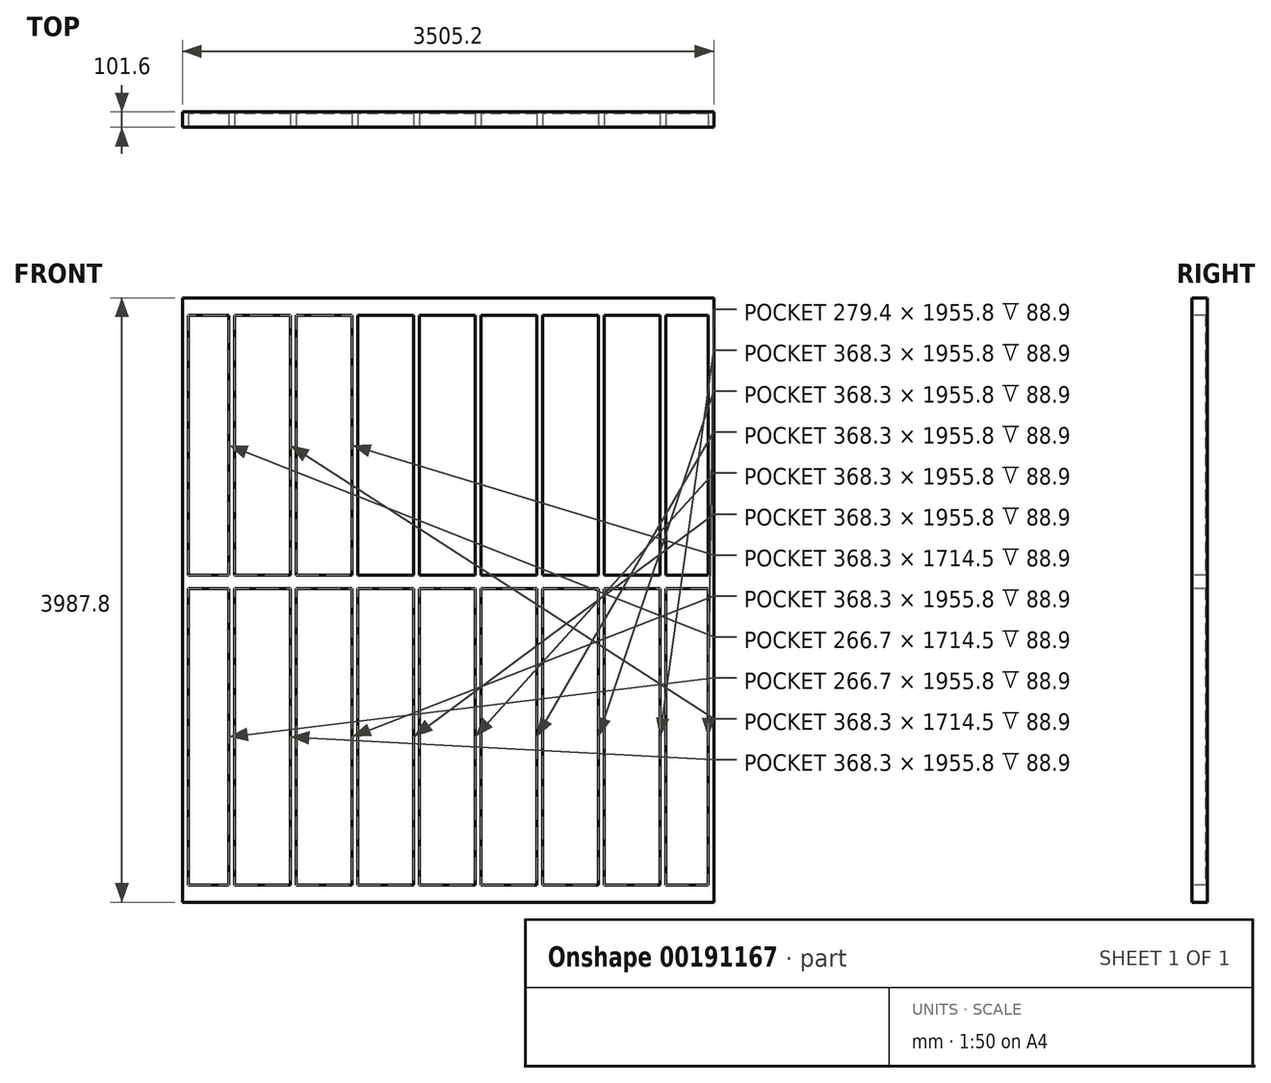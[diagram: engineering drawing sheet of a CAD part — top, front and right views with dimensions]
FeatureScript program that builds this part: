
annotation { "Feature Type Name" : "Feature", "Feature Type Description" : "" }
export const myFeature = defineFeature(function(context is Context, id is Id, definition is map)
    precondition{}
    {
        {
            var Q0;
            Q0=qCreatedBy(makeId("Top.planeOp"),FACE);
            var sketch = newSketch(context, id + "F0", { "sketchPlane" : qUnion([Q0])});
            skLineSegment(sketch, "E0.bottom", {"start": v(1752.6, -44.45) * mm, "end": v(-1752.6, -44.45) * mm});
            skLineSegment(sketch, "E0.top", {"start": v(1752.6, 44.45) * mm, "end": v(-1752.6, 44.45) * mm});
            skLineSegment(sketch, "E0.left", {"start": v(1752.6, -44.45) * mm, "end": v(1752.6, 44.45) * mm});
            skLineSegment(sketch, "E0.right", {"start": v(-1752.6, -44.45) * mm, "end": v(-1752.6, 44.45) * mm});
            skPoint(sketch, "E0.middle", {"position": v(0, 0) * mm});
            skSolve(sketch);
        }
        {
            var Q0;
            Q0 = qSketchRegion(id + "F0", true);
            extrude(context, id + "F1", {"entities" : qUnion([Q0]), "depth" : 38.1 * mm});
        }
        {
            var Q0;
            Q0=makeQuery(id+"F1.opExtrude","CAP_FACE",FACE,{"disambiguationData":[OSD([sQuery(id+"F0.wireOp",EDGE,"E0.bottom"),sQuery(id+"F0.wireOp",EDGE,"E0.top"),sQuery(id+"F0.wireOp",EDGE,"E0.left"),sQuery(id+"F0.wireOp",EDGE,"E0.right")])],"isStart":false});
            var sketch = newSketch(context, id + "F2", { "sketchPlane" : qUnion([Q0])});
            skLineSegment(sketch, "E1.bottom", {"start": v(1752.6, 44.45) * mm, "end": v(1714.5, 44.45) * mm});
            skLineSegment(sketch, "E1.top", {"start": v(1752.6, -44.45) * mm, "end": v(1714.5, -44.45) * mm});
            skLineSegment(sketch, "E1.left", {"start": v(1752.6, 44.45) * mm, "end": v(1752.6, -44.45) * mm});
            skLineSegment(sketch, "E1.right", {"start": v(1714.5, 44.45) * mm, "end": v(1714.5, -44.45) * mm});
            skLineSegment(sketch, "E2.bottom", {"start": v(1435.1, 44.45) * mm, "end": v(1397, 44.45) * mm});
            skLineSegment(sketch, "E2.top", {"start": v(1435.1, -44.45) * mm, "end": v(1397, -44.45) * mm});
            skLineSegment(sketch, "E2.left", {"start": v(1435.1, 44.45) * mm, "end": v(1435.1, -44.45) * mm});
            skLineSegment(sketch, "E2.right", {"start": v(1397, 44.45) * mm, "end": v(1397, -44.45) * mm});
            skLineSegment(sketch, "E3.bottom", {"start": v(1028.7, 44.45) * mm, "end": v(990.6, 44.45) * mm});
            skLineSegment(sketch, "E3.top", {"start": v(1028.7, -44.45) * mm, "end": v(990.6, -44.45) * mm});
            skLineSegment(sketch, "E3.left", {"start": v(1028.7, 44.45) * mm, "end": v(1028.7, -44.45) * mm});
            skLineSegment(sketch, "E3.right", {"start": v(990.6, 44.45) * mm, "end": v(990.6, -44.45) * mm});
            skLineSegment(sketch, "E4.bottom", {"start": v(622.3, 44.45) * mm, "end": v(584.2, 44.45) * mm});
            skLineSegment(sketch, "E4.top", {"start": v(622.3, -44.45) * mm, "end": v(584.2, -44.45) * mm});
            skLineSegment(sketch, "E4.left", {"start": v(622.3, 44.45) * mm, "end": v(622.3, -44.45) * mm});
            skLineSegment(sketch, "E4.right", {"start": v(584.2, 44.45) * mm, "end": v(584.2, -44.45) * mm});
            skLineSegment(sketch, "E5.bottom", {"start": v(215.9, 44.45) * mm, "end": v(177.8, 44.45) * mm});
            skLineSegment(sketch, "E5.top", {"start": v(215.9, -44.45) * mm, "end": v(177.8, -44.45) * mm});
            skLineSegment(sketch, "E5.left", {"start": v(215.9, 44.45) * mm, "end": v(215.9, -44.45) * mm});
            skLineSegment(sketch, "E5.right", {"start": v(177.8, 44.45) * mm, "end": v(177.8, -44.45) * mm});
            skLineSegment(sketch, "E6.bottom", {"start": v(-190.5, 44.45) * mm, "end": v(-228.6, 44.45) * mm});
            skLineSegment(sketch, "E6.top", {"start": v(-190.5, -44.45) * mm, "end": v(-228.6, -44.45) * mm});
            skLineSegment(sketch, "E6.left", {"start": v(-190.5, 44.45) * mm, "end": v(-190.5, -44.45) * mm});
            skLineSegment(sketch, "E6.right", {"start": v(-228.6, 44.45) * mm, "end": v(-228.6, -44.45) * mm});
            skLineSegment(sketch, "E7.bottom", {"start": v(-596.9, 44.45) * mm, "end": v(-635, 44.45) * mm});
            skLineSegment(sketch, "E7.top", {"start": v(-596.9, -44.45) * mm, "end": v(-635, -44.45) * mm});
            skLineSegment(sketch, "E7.left", {"start": v(-596.9, 44.45) * mm, "end": v(-596.9, -44.45) * mm});
            skLineSegment(sketch, "E7.right", {"start": v(-635, 44.45) * mm, "end": v(-635, -44.45) * mm});
            skLineSegment(sketch, "E8.bottom", {"start": v(-1003.3, 44.45) * mm, "end": v(-1041.4, 44.45) * mm});
            skLineSegment(sketch, "E8.top", {"start": v(-1003.3, -44.45) * mm, "end": v(-1041.4, -44.45) * mm});
            skLineSegment(sketch, "E8.left", {"start": v(-1003.3, 44.45) * mm, "end": v(-1003.3, -44.45) * mm});
            skLineSegment(sketch, "E8.right", {"start": v(-1041.4, 44.45) * mm, "end": v(-1041.4, -44.45) * mm});
            skLineSegment(sketch, "E9.bottom", {"start": v(-1752.6, 44.45) * mm, "end": v(-1714.5, 44.45) * mm});
            skLineSegment(sketch, "E9.top", {"start": v(-1752.6, -44.45) * mm, "end": v(-1714.5, -44.45) * mm});
            skLineSegment(sketch, "E9.left", {"start": v(-1752.6, 44.45) * mm, "end": v(-1752.6, -44.45) * mm});
            skLineSegment(sketch, "E9.right", {"start": v(-1714.5, 44.45) * mm, "end": v(-1714.5, -44.45) * mm});
            skLineSegment(sketch, "E10.bottom", {"start": v(-1447.8, 44.45) * mm, "end": v(-1409.7, 44.45) * mm});
            skLineSegment(sketch, "E10.top", {"start": v(-1447.8, -44.45) * mm, "end": v(-1409.7, -44.45) * mm});
            skLineSegment(sketch, "E10.left", {"start": v(-1447.8, 44.45) * mm, "end": v(-1447.8, -44.45) * mm});
            skLineSegment(sketch, "E10.right", {"start": v(-1409.7, 44.45) * mm, "end": v(-1409.7, -44.45) * mm});
            skSolve(sketch);
        }
        {
            var Q0;
            Q0 = qSketchRegion(id + "F2", true);
            extrude(context, id + "F3", {"entities" : qUnion([Q0]), "operationType" : NewBodyOperationType.ADD, "depth" : 3759.2 * mm});
        }
        {
            var Q0;
            Q0=makeQuery(id+"F1.opExtrude","CAP_FACE",FACE,{"disambiguationData":[OSD([sQuery(id+"F0.wireOp",EDGE,"E0.bottom"),sQuery(id+"F0.wireOp",EDGE,"E0.top"),sQuery(id+"F0.wireOp",EDGE,"E0.left"),sQuery(id+"F0.wireOp",EDGE,"E0.right")])],"isStart":true});
            var sketch = newSketch(context, id + "F4", { "sketchPlane" : qUnion([Q0])});
            skLineSegment(sketch, "E11.bottom", {"start": v(1752.6, -44.45) * mm, "end": v(-1752.6, -44.45) * mm});
            skLineSegment(sketch, "E11.top", {"start": v(1752.6, 44.45) * mm, "end": v(-1752.6, 44.45) * mm});
            skLineSegment(sketch, "E11.left", {"start": v(1752.6, -44.45) * mm, "end": v(1752.6, 44.45) * mm});
            skLineSegment(sketch, "E11.right", {"start": v(-1752.6, -44.45) * mm, "end": v(-1752.6, 44.45) * mm});
            skSolve(sketch);
        }
        {
            var Q0;
            Q0 = qSketchRegion(id + "F4", true);
            extrude(context, id + "F5", {"entities" : qUnion([Q0]), "operationType" : NewBodyOperationType.ADD, "depth" : 76.2 * mm});
        }
        {
            var Q0;
            Q0=makeQuery(id+"F5.boolean.opBoolean","MERGE",FACE,{"derivedFrom":[makeQuery(id+"F3.boolean.opBoolean","MERGE",FACE,{"derivedFrom":[makeQuery(id+"F1.opExtrude","SWEPT_FACE",FACE,{"disambiguationData":[OSD([sQuery(id+"F0.wireOp",EDGE,"E0.top")])]}),makeQuery(id+"F3.opExtrude","SWEPT_FACE",FACE,{"disambiguationData":[OSD([sQuery(id+"F2.wireOp",EDGE,"E1.bottom")])]}),makeQuery(id+"F3.opExtrude","SWEPT_FACE",FACE,{"disambiguationData":[OSD([sQuery(id+"F2.wireOp",EDGE,"E2.bottom")])]}),makeQuery(id+"F3.opExtrude","SWEPT_FACE",FACE,{"disambiguationData":[OSD([sQuery(id+"F2.wireOp",EDGE,"E3.bottom")])]}),makeQuery(id+"F3.opExtrude","SWEPT_FACE",FACE,{"disambiguationData":[OSD([sQuery(id+"F2.wireOp",EDGE,"E4.bottom")])]}),makeQuery(id+"F3.opExtrude","SWEPT_FACE",FACE,{"disambiguationData":[OSD([sQuery(id+"F2.wireOp",EDGE,"E5.bottom")])]}),makeQuery(id+"F3.opExtrude","SWEPT_FACE",FACE,{"disambiguationData":[OSD([sQuery(id+"F2.wireOp",EDGE,"E6.bottom")])]}),makeQuery(id+"F3.opExtrude","SWEPT_FACE",FACE,{"disambiguationData":[OSD([sQuery(id+"F2.wireOp",EDGE,"E7.bottom")])]}),makeQuery(id+"F3.opExtrude","SWEPT_FACE",FACE,{"disambiguationData":[OSD([sQuery(id+"F2.wireOp",EDGE,"E8.bottom")])]}),makeQuery(id+"F3.opExtrude","SWEPT_FACE",FACE,{"disambiguationData":[OSD([sQuery(id+"F2.wireOp",EDGE,"E9.bottom")])]}),makeQuery(id+"F3.opExtrude","SWEPT_FACE",FACE,{"disambiguationData":[OSD([sQuery(id+"F2.wireOp",EDGE,"E10.bottom")])]})]}),makeQuery(id+"F5.opExtrude","SWEPT_FACE",FACE,{"disambiguationData":[OSD([sQuery(id+"F4.wireOp",EDGE,"E11.bottom")])]})]});
            var sketch = newSketch(context, id + "F6", { "sketchPlane" : qUnion([Q0])});
            skLineSegment(sketch, "E12.bottom", {"start": v(1752.6, 3797.3) * mm, "end": v(-1752.6, 3797.3) * mm});
            skLineSegment(sketch, "E12.top", {"start": v(1752.6, 3835.4) * mm, "end": v(-1752.6, 3835.4) * mm});
            skLineSegment(sketch, "E12.left", {"start": v(1752.6, 3797.3) * mm, "end": v(1752.6, 3835.4) * mm});
            skLineSegment(sketch, "E12.right", {"start": v(-1752.6, 3797.3) * mm, "end": v(-1752.6, 3835.4) * mm});
            skSolve(sketch);
        }
        {
            var Q0;
            Q0 = qSketchRegion(id + "F6", true);
            extrude(context, id + "F7", {"entities" : qUnion([Q0]), "operationType" : NewBodyOperationType.ADD, "oppositeDirection" : true, "depth" : 88.9 * mm});
        }
        {
            var Q0;
            Q0=makeQuery(id+"F7.opExtrude","SWEPT_FACE",FACE,{"disambiguationData":[OSD([sQuery(id+"F6.wireOp",EDGE,"E12.top")])]});
            var sketch = newSketch(context, id + "F8", { "sketchPlane" : qUnion([Q0])});
            skLineSegment(sketch, "E13.bottom", {"start": v(-1752.6, -44.45) * mm, "end": v(1752.6, -44.45) * mm});
            skLineSegment(sketch, "E13.top", {"start": v(-1752.6, 44.45) * mm, "end": v(1752.6, 44.45) * mm});
            skLineSegment(sketch, "E13.left", {"start": v(-1752.6, -44.45) * mm, "end": v(-1752.6, 44.45) * mm});
            skLineSegment(sketch, "E13.right", {"start": v(1752.6, -44.45) * mm, "end": v(1752.6, 44.45) * mm});
            skSolve(sketch);
        }
        {
            var Q0;
            Q0 = qSketchRegion(id + "F8", true);
            extrude(context, id + "F9", {"entities" : qUnion([Q0]), "operationType" : NewBodyOperationType.ADD, "depth" : 76.2 * mm});
        }
        {
            var Q0;
            Q0=makeQuery(id+"F9.boolean.opBoolean","MERGE",FACE,{"derivedFrom":[makeQuery(id+"F7.boolean.opBoolean","MERGE",FACE,{"derivedFrom":[makeQuery(id+"F5.boolean.opBoolean","MERGE",FACE,{"derivedFrom":[makeQuery(id+"F3.boolean.opBoolean","MERGE",FACE,{"derivedFrom":[makeQuery(id+"F1.opExtrude","SWEPT_FACE",FACE,{"disambiguationData":[OSD([sQuery(id+"F0.wireOp",EDGE,"E0.bottom")])]}),makeQuery(id+"F3.opExtrude","SWEPT_FACE",FACE,{"disambiguationData":[OSD([sQuery(id+"F2.wireOp",EDGE,"E1.top")])]}),makeQuery(id+"F3.opExtrude","SWEPT_FACE",FACE,{"disambiguationData":[OSD([sQuery(id+"F2.wireOp",EDGE,"E2.top")])]}),makeQuery(id+"F3.opExtrude","SWEPT_FACE",FACE,{"disambiguationData":[OSD([sQuery(id+"F2.wireOp",EDGE,"E3.top")])]}),makeQuery(id+"F3.opExtrude","SWEPT_FACE",FACE,{"disambiguationData":[OSD([sQuery(id+"F2.wireOp",EDGE,"E4.top")])]}),makeQuery(id+"F3.opExtrude","SWEPT_FACE",FACE,{"disambiguationData":[OSD([sQuery(id+"F2.wireOp",EDGE,"E5.top")])]}),makeQuery(id+"F3.opExtrude","SWEPT_FACE",FACE,{"disambiguationData":[OSD([sQuery(id+"F2.wireOp",EDGE,"E6.top")])]}),makeQuery(id+"F3.opExtrude","SWEPT_FACE",FACE,{"disambiguationData":[OSD([sQuery(id+"F2.wireOp",EDGE,"E7.top")])]}),makeQuery(id+"F3.opExtrude","SWEPT_FACE",FACE,{"disambiguationData":[OSD([sQuery(id+"F2.wireOp",EDGE,"E8.top")])]}),makeQuery(id+"F3.opExtrude","SWEPT_FACE",FACE,{"disambiguationData":[OSD([sQuery(id+"F2.wireOp",EDGE,"E9.top")])]}),makeQuery(id+"F3.opExtrude","SWEPT_FACE",FACE,{"disambiguationData":[OSD([sQuery(id+"F2.wireOp",EDGE,"E10.top")])]})]}),makeQuery(id+"F5.opExtrude","SWEPT_FACE",FACE,{"disambiguationData":[OSD([sQuery(id+"F4.wireOp",EDGE,"E11.top")])]})]}),makeQuery(id+"F7.opExtrude","CAP_FACE",FACE,{"disambiguationData":[OSD([sQuery(id+"F6.wireOp",EDGE,"E12.bottom"),sQuery(id+"F6.wireOp",EDGE,"E12.top"),sQuery(id+"F6.wireOp",EDGE,"E12.left"),sQuery(id+"F6.wireOp",EDGE,"E12.right")])],"isStart":false})]}),makeQuery(id+"F9.opExtrude","SWEPT_FACE",FACE,{"disambiguationData":[OSD([sQuery(id+"F8.wireOp",EDGE,"E13.bottom")])]})]});
            var sketch = newSketch(context, id + "F10", { "sketchPlane" : qUnion([Q0])});
            skLineSegment(sketch, "E14.bottom", {"start": v(1752.6, 1993.9) * mm, "end": v(-1752.6, 1993.9) * mm});
            skLineSegment(sketch, "E14.top", {"start": v(1752.6, 2082.8) * mm, "end": v(-1752.6, 2082.8) * mm});
            skLineSegment(sketch, "E14.left", {"start": v(1752.6, 1993.9) * mm, "end": v(1752.6, 2082.8) * mm});
            skLineSegment(sketch, "E14.right", {"start": v(-1752.6, 1993.9) * mm, "end": v(-1752.6, 2082.8) * mm});
            skSolve(sketch);
        }
        {
            var Q0;
            Q0 = qSketchRegion(id + "F10", true);
            extrude(context, id + "F11", {"entities" : qUnion([Q0]), "operationType" : NewBodyOperationType.ADD, "oppositeDirection" : true, "depth" : 88.9 * mm});
        }
        {
            var Q0;
            Q0=makeQuery(id+"F11.boolean.opBoolean","MERGE",FACE,{"derivedFrom":[makeQuery(id+"F9.boolean.opBoolean","MERGE",FACE,{"derivedFrom":[makeQuery(id+"F7.boolean.opBoolean","MERGE",FACE,{"derivedFrom":[makeQuery(id+"F5.boolean.opBoolean","MERGE",FACE,{"derivedFrom":[makeQuery(id+"F3.boolean.opBoolean","MERGE",FACE,{"derivedFrom":[makeQuery(id+"F1.opExtrude","SWEPT_FACE",FACE,{"disambiguationData":[OSD([sQuery(id+"F0.wireOp",EDGE,"E0.top")])]}),makeQuery(id+"F3.opExtrude","SWEPT_FACE",FACE,{"disambiguationData":[OSD([sQuery(id+"F2.wireOp",EDGE,"E1.bottom")])]}),makeQuery(id+"F3.opExtrude","SWEPT_FACE",FACE,{"disambiguationData":[OSD([sQuery(id+"F2.wireOp",EDGE,"E2.bottom")])]}),makeQuery(id+"F3.opExtrude","SWEPT_FACE",FACE,{"disambiguationData":[OSD([sQuery(id+"F2.wireOp",EDGE,"E3.bottom")])]}),makeQuery(id+"F3.opExtrude","SWEPT_FACE",FACE,{"disambiguationData":[OSD([sQuery(id+"F2.wireOp",EDGE,"E4.bottom")])]}),makeQuery(id+"F3.opExtrude","SWEPT_FACE",FACE,{"disambiguationData":[OSD([sQuery(id+"F2.wireOp",EDGE,"E5.bottom")])]}),makeQuery(id+"F3.opExtrude","SWEPT_FACE",FACE,{"disambiguationData":[OSD([sQuery(id+"F2.wireOp",EDGE,"E6.bottom")])]}),makeQuery(id+"F3.opExtrude","SWEPT_FACE",FACE,{"disambiguationData":[OSD([sQuery(id+"F2.wireOp",EDGE,"E7.bottom")])]}),makeQuery(id+"F3.opExtrude","SWEPT_FACE",FACE,{"disambiguationData":[OSD([sQuery(id+"F2.wireOp",EDGE,"E8.bottom")])]}),makeQuery(id+"F3.opExtrude","SWEPT_FACE",FACE,{"disambiguationData":[OSD([sQuery(id+"F2.wireOp",EDGE,"E9.bottom")])]}),makeQuery(id+"F3.opExtrude","SWEPT_FACE",FACE,{"disambiguationData":[OSD([sQuery(id+"F2.wireOp",EDGE,"E10.bottom")])]})]}),makeQuery(id+"F5.opExtrude","SWEPT_FACE",FACE,{"disambiguationData":[OSD([sQuery(id+"F4.wireOp",EDGE,"E11.bottom")])]})]}),makeQuery(id+"F7.opExtrude","CAP_FACE",FACE,{"disambiguationData":[OSD([sQuery(id+"F6.wireOp",EDGE,"E12.bottom"),sQuery(id+"F6.wireOp",EDGE,"E12.top"),sQuery(id+"F6.wireOp",EDGE,"E12.left"),sQuery(id+"F6.wireOp",EDGE,"E12.right")])],"isStart":true})]}),makeQuery(id+"F9.opExtrude","SWEPT_FACE",FACE,{"disambiguationData":[OSD([sQuery(id+"F8.wireOp",EDGE,"E13.top")])]})]}),makeQuery(id+"F11.opExtrude","CAP_FACE",FACE,{"disambiguationData":[OSD([sQuery(id+"F10.wireOp",EDGE,"E14.bottom"),sQuery(id+"F10.wireOp",EDGE,"E14.top"),sQuery(id+"F10.wireOp",EDGE,"E14.left"),sQuery(id+"F10.wireOp",EDGE,"E14.right")])],"isStart":false})]});
            var sketch = newSketch(context, id + "F12", { "sketchPlane" : qUnion([Q0])});
            skLineSegment(sketch, "E15.bottom", {"start": v(-1752.6, 3911.6) * mm, "end": v(1752.6, 3911.6) * mm});
            skLineSegment(sketch, "E15.top", {"start": v(-1752.6, -76.2) * mm, "end": v(1752.6, -76.2) * mm});
            skLineSegment(sketch, "E15.left", {"start": v(-1752.6, 3911.6) * mm, "end": v(-1752.6, -76.2) * mm});
            skLineSegment(sketch, "E15.right", {"start": v(1752.6, 3911.6) * mm, "end": v(1752.6, -76.2) * mm});
            skSolve(sketch);
        }
        {
            var Q0;
            Q0 = qSketchRegion(id + "F12", true);
            extrude(context, id + "F13", {"entities" : qUnion([Q0]), "operationType" : NewBodyOperationType.ADD, "depth" : 12.7 * mm});
        }
    });
